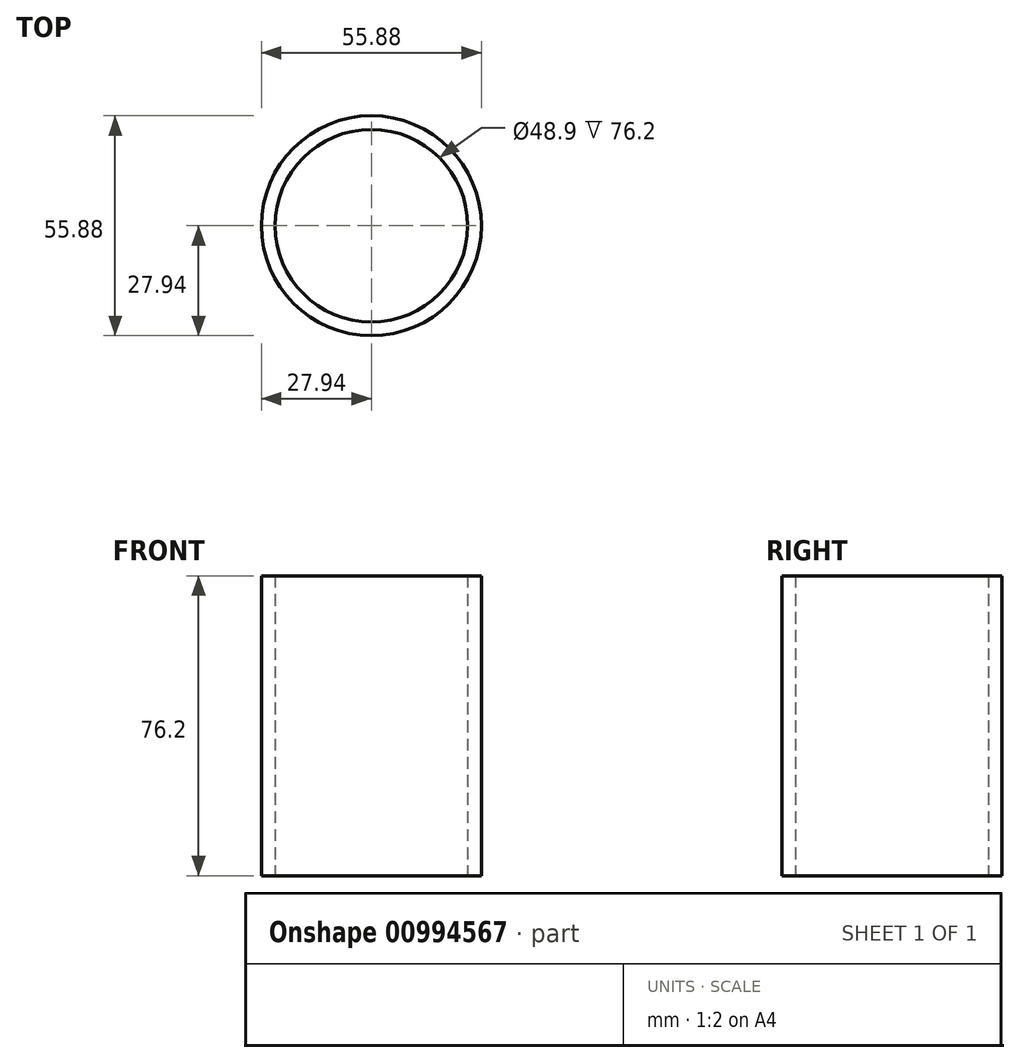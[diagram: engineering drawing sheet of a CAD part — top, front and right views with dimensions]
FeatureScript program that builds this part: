
annotation { "Feature Type Name" : "Feature", "Feature Type Description" : "" }
export const myFeature = defineFeature(function(context is Context, id is Id, definition is map)
    precondition{}
    {
        {
            var Q0;
            Q0=qCreatedBy(makeId("Top.planeOp"),FACE);
            var sketch = newSketch(context, id + "F0", { "sketchPlane" : qUnion([Q0])});
            skCircle(sketch, "E0", {"center": v(0, 0) * mm, "radius": 24.45 * mm});
            skCircle(sketch, "E1", {"center": v(0, 0) * mm, "radius": 27.94 * mm});
            skSolve(sketch);
        }
        {
            var Q0;
            Q0 = qSketchRegion(id + "F0", true);
            extrude(context, id + "F1", {"entities" : qUnion([Q0]), "depth" : 76.2 * mm, "offsetDistance" : 25.4 * mm});
        }
    });
